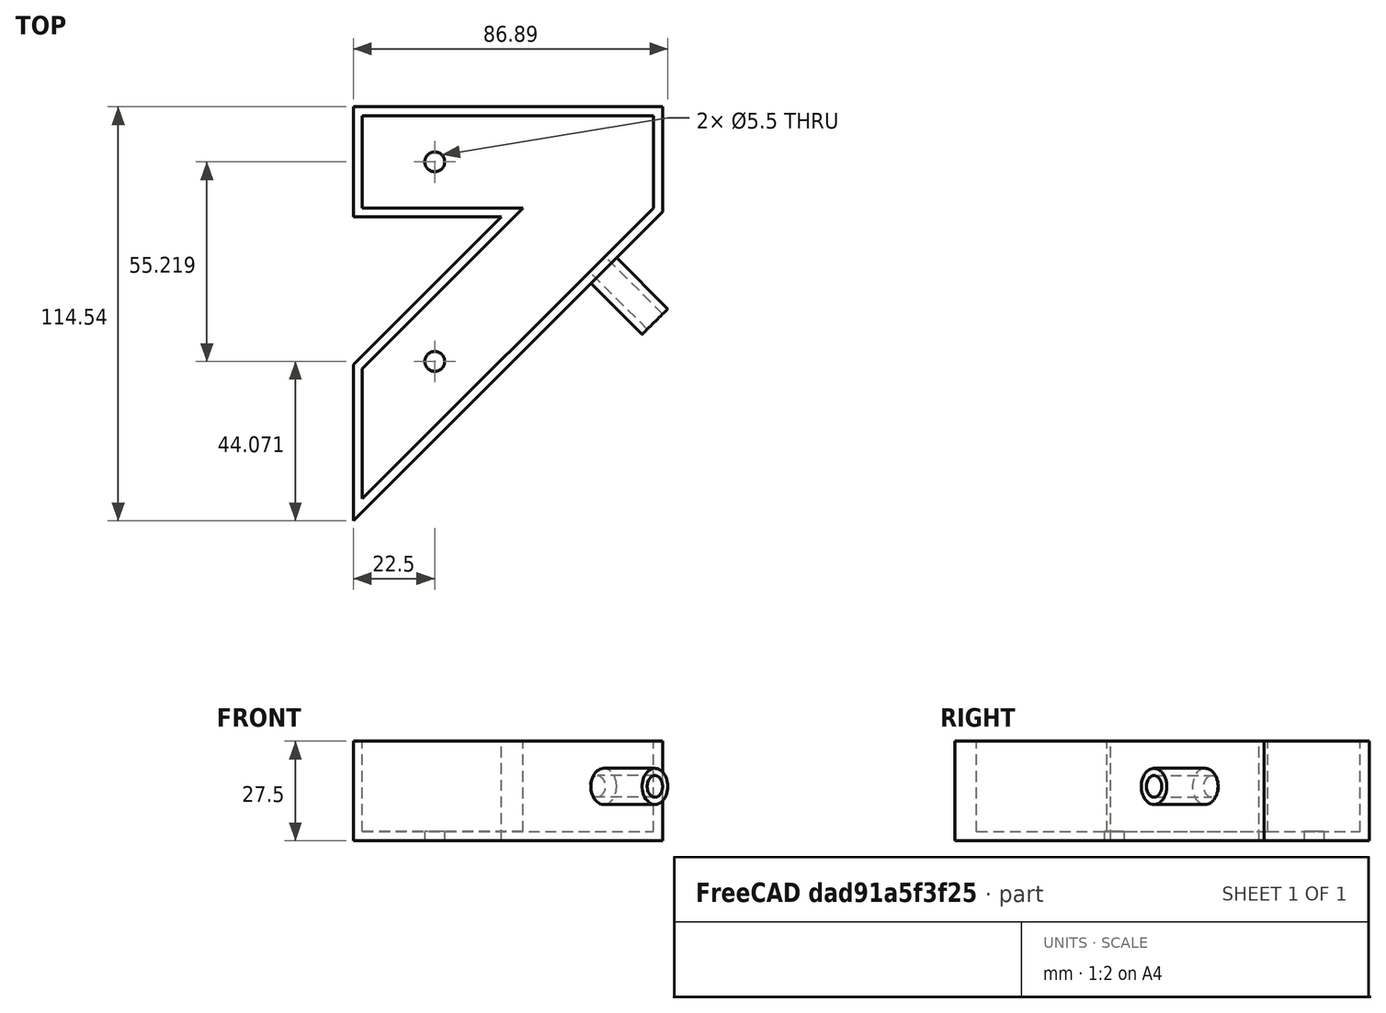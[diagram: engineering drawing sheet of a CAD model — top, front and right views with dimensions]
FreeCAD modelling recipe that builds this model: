
FCSTD DOCUMENT  (FreeCAD 0.18R4 (GitTag))
Label: jig
License: All rights reserved
LicenseURL: http://en.wikipedia.org/wiki/All_rights_reserved
objects: Sketcher::SketchObject×5, PartDesign::Pad×3, Spreadsheet::Sheet×1, PartDesign::Plane×1, PartDesign::Hole×1, PartDesign::Pocket×1, PartDesign::Body×1, Mesh::Feature×1
note: 17 computed .brp shape members not serialized (recipe doc carries the construction recipe); baked Part::Feature solids carry a one-line shape summary decoded from their .brp

FEATURE [Sketcher::SketchObject] Sketch
  MapMode = 5
  Support = -> [XY_Plane001]
  expr: Constraints[49] = Dim.thickness
  expr: Constraints[39] = Dim.thickness
  expr: Constraints[36] = Dim.thickness
  expr: Constraints[37] = Dim.thickness
  expr: Constraints[35] = Dim.thickness
  expr: Constraints[17] = Dim.profile_slack
  expr: Constraints[44] = Dim.thickness
  expr: Constraints[16] = Dim.profile_slack
  expr: Constraints[38] = Dim.thickness
  expr: Constraints[3] = Dim.length_slack
  sketch-geometry (17):
    g0: LineSegment StartX=80.5 StartY=25.5 StartZ=0 EndX=0 EndY=25.5 EndZ=0
    g1: LineSegment StartX=0 StartY=25.5 StartZ=0 EndX=0 EndY=0 EndZ=0
    g2: LineSegment StartX=80.5 StartY=25.5 StartZ=0 EndX=80.5 EndY=0 EndZ=0
    g3: LineSegment StartX=0 StartY=0 StartZ=0 EndX=44.4376 EndY=0 EndZ=0
    g4: LineSegment StartX=80.5 StartY=0 StartZ=0 EndX=0 EndY=-80.5 EndZ=0
    g5: LineSegment StartX=44.4376 StartY=0 StartZ=0 EndX=0 EndY=-44.4376 EndZ=0
    g6: LineSegment [constr] StartX=44.4376 StartY=0 StartZ=0 EndX=62.4688 EndY=-18.0312 EndZ=0
    g7: LineSegment StartX=0 StartY=-44.4376 StartZ=0 EndX=0 EndY=-80.5 EndZ=0
    g8: LineSegment StartX=-2.5 StartY=28 StartZ=0 EndX=83 EndY=28 EndZ=0
    g9: LineSegment StartX=83 StartY=28 StartZ=0 EndX=83 EndY=-1.03553 EndZ=0
    g10: LineSegment StartX=83 StartY=-1.03553 StartZ=0 EndX=-2.5 EndY=-86.5355 EndZ=0
    g11: LineSegment StartX=-2.5 StartY=-86.5355 StartZ=0 EndX=-2.5 EndY=-43.402 EndZ=0
    g12: LineSegment StartX=-2.5 StartY=-43.402 StartZ=0 EndX=38.402 EndY=-2.5 EndZ=0
    g13: LineSegment StartX=38.402 StartY=-2.5 StartZ=0 EndX=-2.5 EndY=-2.5 EndZ=0
    g14: LineSegment StartX=-2.5 StartY=-2.5 StartZ=0 EndX=-2.5 EndY=28 EndZ=0
    g15: LineSegment [constr] StartX=38.402 StartY=-2.5 StartZ=0 EndX=40.1698 EndY=-4.26777 EndZ=0
    g16: LineSegment [constr] StartX=62.4688 StartY=-18.0312 StartZ=0 EndX=64.2365 EndY=-19.799 EndZ=0
  constraints (50):
    c: Coincident(g0,g1)
    c: Horizontal(g0)
    c: Vertical(g1)
    c: DistanceX(g0,g0) = 80.5
    c: PointOnObject(g2,g-1)
    c: Vertical(g2)
    c: PointOnObject(g3,g-1)
    c: Coincident(g4,g2)
    c: DistanceX(g1,g4) = 0
    c: Angle(g4) = -2.35619
    c: Coincident(g5,g3)
    c: DistanceX(g5,g1) = 0
    c: Angle(g5) = -2.35619
    c: Coincident(g6,g3)
    c: PointOnObject(g6,g4)
    c: Perpendicular(g4,g6)
    c: Distance(g6) = 25.5
    c: DistanceY(g2,g2) = 25.5
    c: Coincident(g0,g2)
    c: Coincident(g3,g1)
    c: Coincident(g1,g-1)
    c: Coincident(g7,g5)
    c: Coincident(g7,g4)
    c: Horizontal(g8)
    c: Coincident(g8,g9)
    c: Vertical(g9)
    c: Coincident(g9,g10)
    c: Coincident(g10,g11)
    c: Vertical(g11)
    c: Coincident(g11,g12)
    c: Coincident(g12,g13)
    c: Horizontal(g13)
    c: Coincident(g13,g14)
    c: Vertical(g14)
    c: Coincident(g14,g8)
    c: DistanceX(g0,g8) = 2.5
    c: DistanceY(g0,g8) = 2.5
    c: DistanceX(g8,g0) = 2.5
    c: DistanceY(g13,g1) = 2.5
    c: DistanceX(g11,g5) = 2.5
    c: Angle(g12) = 0.785398
    c: Coincident(g15,g12)
    c: PointOnObject(g15,g5)
    c: Perpendicular(g5,g15)
    c: Distance(g15) = 2.5
    c: Angle(g10) = -2.35619
    c: Coincident(g16,g6)
    c: PointOnObject(g16,g10)
    c: Perpendicular(g10,g16)
    c: Distance(g16) = 2.5
FEATURE [Spreadsheet::Sheet] Spreadsheet  label="Dim"
  cells = A1=profile; B1(profile)=25; A2=slack; B2(slack)=0.5; A3=length; B3(length)=80; A4=thickness; B4(thickness)=2.5; A5=hole_angle; B5(hole_angle)=3.5; A6=hole_mount; B6(hole_mount)=5.5; A7=hole_wall; B7(hole_wall)=2; A8=hole_guide; B8(hole_guide)=20; A9=vertical; B9(vertical)=40; A10=; A11=profile_slack; B11(profile_slack)==profile + slack; A12=length_slack; B12(length_slack)==length + slack
FEATURE [Sketcher::SketchObject] Sketch001
  ExternalGeometry = -> [Sketch]
  MapMode = 5
  Support = -> [XY_Plane001]
  sketch-geometry (7):
    g0: LineSegment StartX=-2.5 StartY=-43.402 StartZ=0 EndX=-2.5 EndY=-86.5355 EndZ=0
    g1: LineSegment StartX=-2.5 StartY=-43.402 StartZ=0 EndX=38.402 EndY=-2.5 EndZ=0
    g2: LineSegment StartX=38.402 StartY=-2.5 StartZ=0 EndX=-2.5 EndY=-2.5 EndZ=0
    g3: LineSegment StartX=-2.5 StartY=-2.5 StartZ=0 EndX=-2.5 EndY=28 EndZ=0
    g4: LineSegment StartX=-2.5 StartY=28 StartZ=0 EndX=83 EndY=28 EndZ=0
    g5: LineSegment StartX=83 StartY=28 StartZ=0 EndX=83 EndY=-1.03553 EndZ=0
    g6: LineSegment StartX=83 StartY=-1.03553 StartZ=0 EndX=-2.5 EndY=-86.5355 EndZ=0
  constraints (14):
    c: Coincident(g0,g-10)
    c: Coincident(g0,g-10)
    c: Coincident(g1,g0)
    c: Coincident(g1,g-8)
    c: Coincident(g2,g1)
    c: Coincident(g2,g-7)
    c: Coincident(g3,g2)
    c: Coincident(g3,g-6)
    c: Coincident(g4,g3)
    c: Coincident(g4,g-6)
    c: Coincident(g5,g4)
    c: Coincident(g5,g-9)
    c: Coincident(g6,g5)
    c: Coincident(g6,g0)
FEATURE [PartDesign::Pad] Pad
  Length = 2.5
  Length2 = 100
  Profile = -> Sketch001
  Refine = true
  Type = 0
  expr: Length = Dim.thickness
FEATURE [PartDesign::Pad] Pad001
  BaseFeature = -> Pad
  Length = 27.5
  Length2 = 100
  Profile = -> Sketch
  Refine = true
  Type = 0
  expr: Length = Dim.thickness + Dim.profile
FEATURE [PartDesign::Plane] DatumPlane
  Length = 162.618
  MapMode = 5
  Placement = pos=(42.0178,-42.0178,0) rot=(0.862856,0.357407,0.357407;1.71777rad)
  ResizeMode = 0
  Support = -> [Pad001]
  Width = 52.3862
FEATURE [Sketcher::SketchObject] Sketch002
  ExternalGeometry = -> [Pad001]
  MapMode = 5
  Placement = pos=(42.0178,-42.0178,0) rot=(0.862856,0.357407,0.357407;1.71777rad)
  Support = -> [DatumPlane]
  expr: Constraints[2] = Dim.hole_angle
  expr: Constraints[1] = Dim.hole_angle
  sketch-geometry (2):
    g0: GeomPoint X=31.4221 Y=15 Z=0
    g1: Circle CenterX=34.9221 CenterY=15 CenterZ=0 NormalX=0 NormalY=0 NormalZ=1 AngleXU=0 Radius=1.75
  constraints (3):
    c: Symmetric(g-3,g-3,g0)
    c: Diameter(g1) = 3.5
    c: DistanceX(g0,g1) = 3.5
FEATURE [PartDesign::Hole] Hole
  BaseFeature = -> Pad001
  Depth = 25
  DepthType = 0
  Diameter = 6
  DrillPoint = 1
  DrillPointAngle = 118
  HoleCutCountersinkAngle = 90
  HoleCutDepth = 0
  HoleCutDiameter = 0
  HoleCutType = 0
  ModelActualThread = false
  Profile = -> Sketch002
  Refine = true
  Tapered = false
  TaperedAngle = 90
  ThreadAngle = 0
  ThreadClass = 0
  ThreadCutOffInner = 0
  ThreadCutOffOuter = 0
  ThreadDirection = 0
  ThreadFit = 0
  ThreadPitch = 0
  ThreadSize = 0
  ThreadType = 0
  Threaded = false
FEATURE [Sketcher::SketchObject] Sketch003
  ExternalGeometry = -> [Hole]
  MapMode = 5
  Placement = pos=(42.0178,-42.0178,0) rot=(0.862856,0.357407,0.357407;1.71777rad)
  Support = -> [DatumPlane]
  expr: Constraints[5] = Dim.hole_wall
  sketch-geometry (3):
    g0: Circle CenterX=34.9221 CenterY=15 CenterZ=0 NormalX=0 NormalY=0 NormalZ=1 AngleXU=0 Radius=3
    g1: Circle CenterX=34.9221 CenterY=15 CenterZ=0 NormalX=0 NormalY=0 NormalZ=1 AngleXU=0 Radius=5
    g2: LineSegment [constr] StartX=36.9122 StartY=12.7551 StartZ=0 EndX=38.2389 EndY=11.2585 EndZ=0
  constraints (7):
    c: Coincident(g0,g-3)
    c: Coincident(g1,g0)
    c: PointOnObject(g2,g0)
    c: PointOnObject(g2,g1)
    c: Perpendicular(g1,g2)
    c: Distance(g2) = 2
    c: PointOnObject(g2,g-3)
FEATURE [PartDesign::Pad] Pad002
  BaseFeature = -> Hole
  Length = 20
  Length2 = 100
  Profile = -> Sketch003
  Refine = true
  Type = 0
  expr: Length = Dim.hole_guide
FEATURE [Sketcher::SketchObject] Sketch004
  ExternalGeometry = -> [Pad002]
  MapMode = 5
  Support = -> [XY_Plane001]
  expr: Constraints[11] = Dim.hole_mount
  expr: Constraints[5] = Dim.vertical / 2
  sketch-geometry (6):
    g0: GeomPoint X=0 Y=12.75 Z=0
    g1: GeomPoint X=0 Y=-62.4688 Z=0
    g2: LineSegment [constr] StartX=0 StartY=12.75 StartZ=0 EndX=20 EndY=12.75 EndZ=0
    g3: LineSegment [constr] StartX=0 StartY=-62.4688 StartZ=0 EndX=20 EndY=-42.4688 EndZ=0
    g4: Circle CenterX=20 CenterY=12.75 CenterZ=0 NormalX=0 NormalY=0 NormalZ=1 AngleXU=0 Radius=2.75
    g5: Circle CenterX=20 CenterY=-42.4688 CenterZ=0 NormalX=0 NormalY=0 NormalZ=1 AngleXU=0 Radius=2.75
  constraints (12):
    c: Horizontal(g2)
    c: Coincident(g3,g1)
    c: Symmetric(g-3,g-3,g0)
    c: Symmetric(g-4,g-4,g1)
    c: Angle(g3) = 0.785398
    c: DistanceX(g-4,g3) = 20
    c: DistanceX(g2,g3) = 0
    c: Coincident(g2,g0)
    c: Coincident(g4,g2)
    c: Coincident(g5,g3)
    c: Equal(g5,g4)
    c: Diameter(g4) = 5.5
FEATURE [PartDesign::Pocket] Pocket
  BaseFeature = -> Pad002
  Length = 5
  Length2 = 100
  Profile = -> Sketch004
  Refine = true
  Reversed = true
  Type = 0
FEATURE [PartDesign::Body] Body001
  Group = -> [Sketch,Sketch001,Pad,Pad001,DatumPlane,Sketch002,Hole,Sketch003,Pad002,Sketch004,Pocket]
  Origin = -> Origin001
  Tip = -> Pocket
FEATURE [Mesh::Feature] Mesh  label="Body001 (Meshed)"
